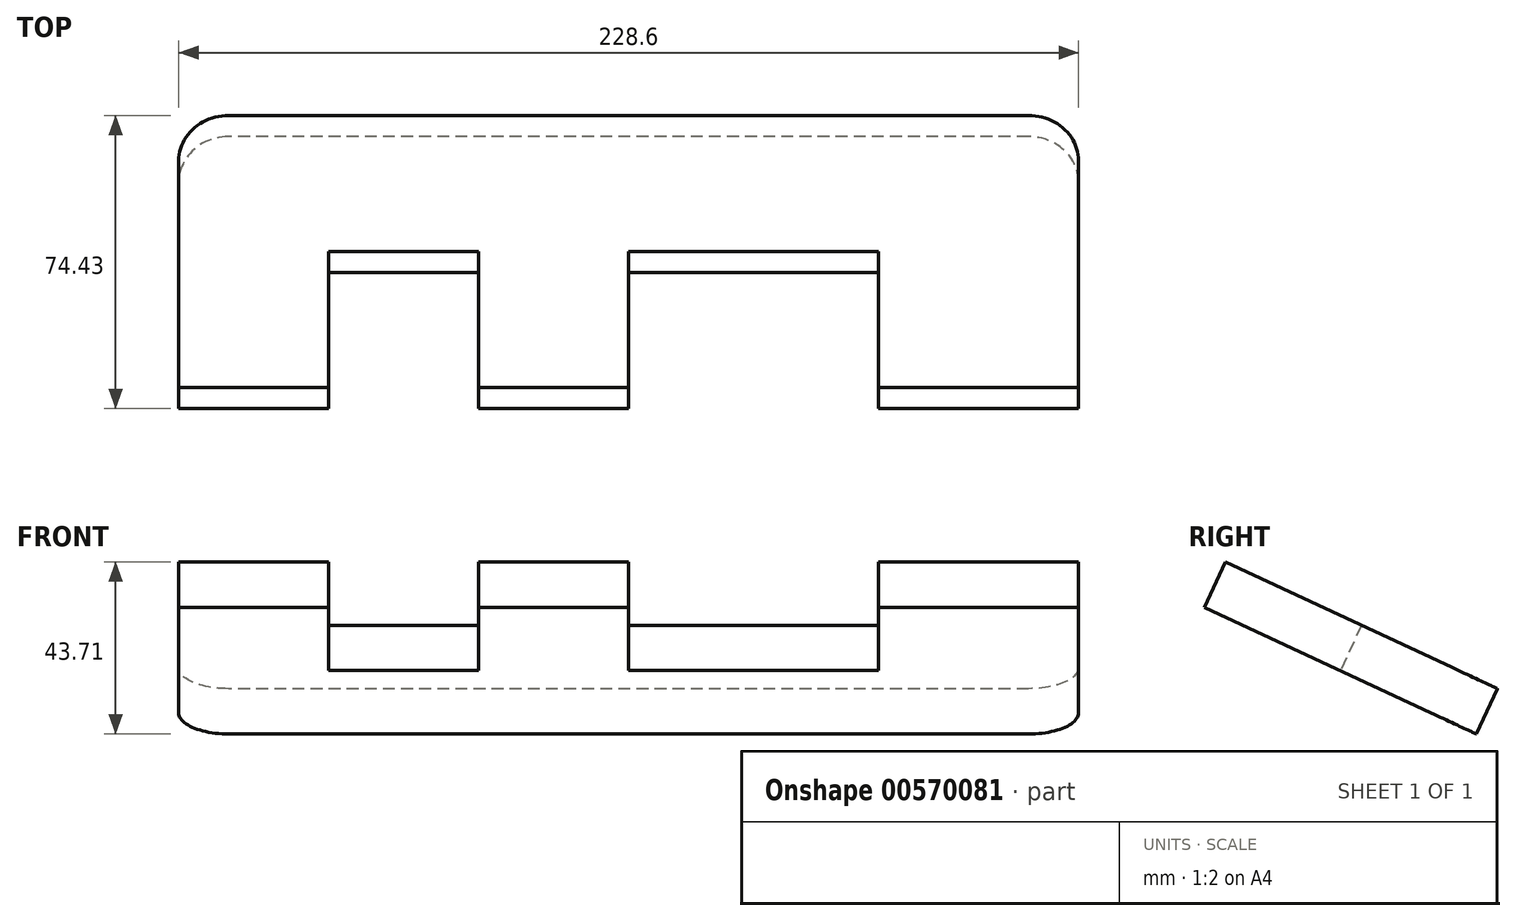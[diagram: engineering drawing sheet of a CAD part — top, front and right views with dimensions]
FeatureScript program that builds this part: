
annotation { "Feature Type Name" : "Feature", "Feature Type Description" : "" }
export const myFeature = defineFeature(function(context is Context, id is Id, definition is map)
    precondition{}
    {
        {
            var Q0;
            Q0=qCreatedBy(makeId("Front.planeOp"),FACE);
            var sketch = newSketch(context, id + "F0", { "sketchPlane" : qUnion([Q0])});
            skLineSegment(sketch, "E0", {"start": v(12.7, 0) * mm, "end": v(215.9, 0) * mm});
            skLineSegment(sketch, "E1", {"start": v(228.6, 12.7) * mm, "end": v(228.6, 76.2) * mm});
            skLineSegment(sketch, "E2", {"start": v(228.6, 76.2) * mm, "end": v(0, 76.2) * mm});
            skLineSegment(sketch, "E3", {"start": v(0, 76.2) * mm, "end": v(0, 12.7) * mm});
            skPoint(sketch, "E4.visualSharp", {"position": v(0, 0) * mm});
            skArc(sketch, "E4.filletArc", {"start": v(0, 12.7) * mm, "mid": v(3.72, 3.72) * mm, "end": v(12.7, 0) * mm});
            skPoint(sketch, "E5.visualSharp", {"position": v(228.6, 0) * mm});
            skArc(sketch, "E5.filletArc", {"start": v(215.9, 0) * mm, "mid": v(224.88, 3.72) * mm, "end": v(228.6, 12.7) * mm});
            skLineSegment(sketch, "E6", {"start": v(228.6, 76.2) * mm, "end": v(190.5, 76.2) * mm});
            skLineSegment(sketch, "E7", {"start": v(0, 76.2) * mm, "end": v(50.8, 76.2) * mm});
            skLineSegment(sketch, "E8", {"start": v(190.5, 76.2) * mm, "end": v(190.5, 38.1) * mm});
            skLineSegment(sketch, "E9", {"start": v(190.5, 38.1) * mm, "end": v(152.4, 38.1) * mm});
            skLineSegment(sketch, "E10", {"start": v(152.4, 38.1) * mm, "end": v(152.4, 76.2) * mm});
            skLineSegment(sketch, "E11", {"start": v(152.4, 76.2) * mm, "end": v(114.3, 76.2) * mm});
            skLineSegment(sketch, "E12", {"start": v(50.8, 76.2) * mm, "end": v(50.8, 38.1) * mm});
            skLineSegment(sketch, "E13", {"start": v(50.8, 38.1) * mm, "end": v(114.3, 38.1) * mm});
            skLineSegment(sketch, "E14", {"start": v(114.3, 76.2) * mm, "end": v(114.3, 38.1) * mm});
            skSolve(sketch);
        }
        {
            var Q0;
            Q0=qSketchRegion(id+"F0",true);
            extrude(context, id + "F1", {"entities" : qUnion([Q0]), "depth" : 12.7 * mm, "offsetDistance" : 25.4 * mm});
        }
        {
            var Q0;
            {var subQ0=sQuery(id+"F0.wireOp",EDGE,"E12");Q0=makeQuery(id+"F0.imprint","IMPRINT",FACE,{"disambiguationData":[TD([[makeQuery(id+"F0.imprint","IMPRINT",EDGE,{"derivedFrom":subQ0}),1.0]])]});}
            var Q1;
            {var subQ0=sQuery(id+"F0.wireOp",EDGE,"E8");Q1=makeQuery(id+"F0.imprint","IMPRINT",FACE,{"disambiguationData":[TD([[makeQuery(id+"F0.imprint","IMPRINT",EDGE,{"derivedFrom":subQ0}),-1.0]])]});}
            extrude(context, id + "F2", {"entities" : qUnion([Q0, Q1]), "operationType" : NewBodyOperationType.REMOVE, "depth" : 12.7 * mm, "offsetDistance" : 25.4 * mm});
        }
        {
            var Q0;
            Q0=makeQuery(id+"F1.opExtrude","SWEPT_BODY",BODY,{"disambiguationData":[OSD([sQuery(id+"F0.wireOp",EDGE,"E0"),sQuery(id+"F0.wireOp",EDGE,"E1"),sQuery(id+"F0.wireOp",EDGE,"E2"),sQuery(id+"F0.wireOp",EDGE,"E3"),sQuery(id+"F0.wireOp",EDGE,"E4.filletArc"),sQuery(id+"F0.wireOp",EDGE,"E5.filletArc"),sQuery(id+"F0.wireOp",EDGE,"E6"),sQuery(id+"F0.wireOp",EDGE,"E7"),sQuery(id+"F0.wireOp",EDGE,"E11")])]});
            var Q1;
            {var subQ0=sQuery(id+"F0.wireOp",EDGE,"E11");var subQ1=sQuery(id+"F0.wireOp",EDGE,"E7");var subQ2=sQuery(id+"F0.wireOp",EDGE,"E6");var subQ3=sQuery(id+"F0.wireOp",EDGE,"E3");var subQ4=sQuery(id+"F0.wireOp",EDGE,"E2");Q1=makeQuery(id+"F2.boolean.opBoolean","SPLIT",EDGE,{"disambiguationData":[TD([makeQuery(id+"F1.opExtrude","SWEPT_FACE",FACE,{"disambiguationData":[OSD([subQ3])]})])],"derivedFrom":makeQuery(id+"F1.opExtrude","CAP_EDGE",EDGE,{"disambiguationData":[OSD([subQ4,subQ2,subQ1,subQ0])],"isStart":false})});}
            var Q2;
            {var subQ0=sQuery(id+"F0.wireOp",EDGE,"E11");var subQ1=sQuery(id+"F0.wireOp",EDGE,"E7");var subQ2=sQuery(id+"F0.wireOp",EDGE,"E6");var subQ3=sQuery(id+"F0.wireOp",EDGE,"E3");var subQ4=sQuery(id+"F0.wireOp",EDGE,"E2");Q2=makeQuery(id+"F2.boolean.opBoolean","SPLIT",EDGE,{"disambiguationData":[TD([makeQuery(id+"F1.opExtrude","SWEPT_FACE",FACE,{"disambiguationData":[OSD([subQ3])]})])],"derivedFrom":makeQuery(id+"F1.opExtrude","CAP_EDGE",EDGE,{"disambiguationData":[OSD([subQ4,subQ2,subQ1,subQ0])],"isStart":false})});}
            transform(context, id + "F3", {"entities" : qUnion([Q0]), "transformType" : TransformType.ROTATION, "transformAxis" : qUnion([Q2]), "angle" : 295 * degree, "makeCopy" : false});
        }
        {
            var Q0;
            Q0=makeQuery(id+"F1.opExtrude","SWEPT_BODY",BODY,{"disambiguationData":[OSD([sQuery(id+"F0.wireOp",EDGE,"E0"),sQuery(id+"F0.wireOp",EDGE,"E1"),sQuery(id+"F0.wireOp",EDGE,"E2"),sQuery(id+"F0.wireOp",EDGE,"E3"),sQuery(id+"F0.wireOp",EDGE,"E4.filletArc"),sQuery(id+"F0.wireOp",EDGE,"E5.filletArc"),sQuery(id+"F0.wireOp",EDGE,"E6"),sQuery(id+"F0.wireOp",EDGE,"E7"),sQuery(id+"F0.wireOp",EDGE,"E11")])]});
            var Q1;
            Q1=makeQuery(id+"F1.opExtrude","CAP_EDGE",EDGE,{"disambiguationData":[OSD([sQuery(id+"F0.wireOp",EDGE,"E3")])],"isStart":false});
            transform(context, id + "F4", {"entities" : qUnion([Q0]), "transformType" : TransformType.ROTATION, "transformAxis" : qUnion([Q1]), "angle" : 180 * degree, "makeCopy" : false});
        }
    });
